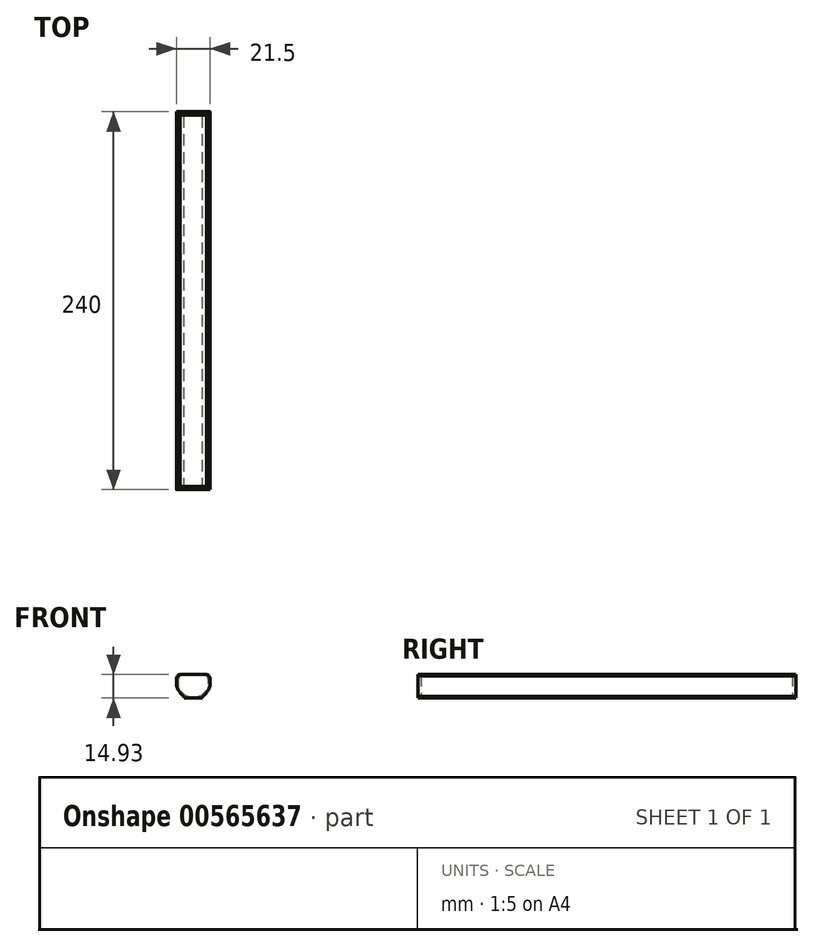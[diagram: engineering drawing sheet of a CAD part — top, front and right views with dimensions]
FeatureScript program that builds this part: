
annotation { "Feature Type Name" : "Feature", "Feature Type Description" : "" }
export const myFeature = defineFeature(function(context is Context, id is Id, definition is map)
    precondition{}
    {
        {
            var Q0;
            Q0=qCreatedBy(makeId("Front.planeOp"),FACE);
            var sketch = newSketch(context, id + "F0", { "sketchPlane" : qUnion([Q0])});
            skLineSegment(sketch, "E0", {"start": v(-4.53, -9.75) * mm, "end": v(4.53, -9.75) * mm});
            skPoint(sketch, "E1", {"position": v(0, -9.75) * mm});
            skArc(sketch, "E2", {"start": v(-8.5, 4.78) * mm, "mid": v(0, -9.75) * mm, "end": v(8.5, 4.78) * mm});
            skArc(sketch, "E3.0", {"start": v(-9.93, 4.1) * mm, "mid": v(-10.01, -3.9) * mm, "end": v(-4.53, -9.75) * mm});
            skArc(sketch, "E4.trimOffspring", {"start": v(4.53, -9.75) * mm, "mid": v(10.01, -3.9) * mm, "end": v(9.93, 4.1) * mm});
            skLineSegment(sketch, "E5", {"start": v(-9.93, 4.1) * mm, "end": v(-8.5, 4.78) * mm});
            skLineSegment(sketch, "E6", {"start": v(8.5, 4.78) * mm, "end": v(9.93, 4.1) * mm});
            skLineSegment(sketch, "E7", {"start": v(-6, -9.75) * mm, "end": v(-6, -8.92) * mm});
            skLineSegment(sketch, "E8", {"start": v(6, -9.75) * mm, "end": v(6, -8.92) * mm});
            skLineSegment(sketch, "E9.top", {"start": v(-6, -10.15) * mm, "end": v(6, -10.15) * mm});
            skLineSegment(sketch, "E9.left", {"start": v(-6, -9.75) * mm, "end": v(-6, -10.15) * mm});
            skLineSegment(sketch, "E9.right", {"start": v(6, -9.75) * mm, "end": v(6, -10.15) * mm});
            skLineSegment(sketch, "E10", {"start": v(-8.5, 4.78) * mm, "end": v(8.5, 4.78) * mm});
            skSolve(sketch);
        }
        {
            var Q0;
            {var subQ0=sQuery(id+"F0.wireOp",EDGE,"E5");Q0=makeQuery(id+"F0.imprint","IMPRINT",FACE,{"disambiguationData":[TD([[makeQuery(id+"F0.imprint","IMPRINT",EDGE,{"derivedFrom":subQ0}),-1.0]])]});}
            var Q1;
            {var subQ0=sQuery(id+"F0.wireOp",EDGE,"E6");Q1=makeQuery(id+"F0.imprint","IMPRINT",FACE,{"disambiguationData":[TD([[makeQuery(id+"F0.imprint","IMPRINT",EDGE,{"derivedFrom":subQ0}),-1.0]])]});}
            var Q2;
            {var subQ7=sQuery(id+"F0.wireOp",EDGE,"E7");Q2=makeQuery(id+"F0.imprint","IMPRINT",FACE,{"disambiguationData":[TD([[makeQuery(id+"F0.imprint","IMPRINT",EDGE,{"derivedFrom":subQ7}),-1.0]])]});}
            extrude(context, id + "F1", {"entities" : qUnion([Q0, Q1, Q2]), "depth" : 240 * mm, "offsetDistance" : 25 * mm});
        }
        {
            var Q0;
            {var subQ2=sQuery(id+"F0.wireOp",EDGE,"E10");Q0=makeQuery(id+"F0.imprint","IMPRINT",FACE,{"disambiguationData":[TD([[makeQuery(id+"F0.imprint","IMPRINT",EDGE,{"derivedFrom":subQ2}),-1.0]])]});}
            extrude(context, id + "F2", {"entities" : qUnion([Q0]), "operationType" : NewBodyOperationType.ADD, "depth" : 2 * mm, "offsetDistance" : 25 * mm});
        }
        {
            var Q0;
            Q0=makeQuery(id+"F1.opExtrude","CAP_FACE",FACE,{"disambiguationData":[OSD([sQuery(id+"F0.wireOp",EDGE,"E2"),sQuery(id+"F0.wireOp",EDGE,"E3.0"),sQuery(id+"F0.wireOp",EDGE,"E4.trimOffspring"),sQuery(id+"F0.wireOp",EDGE,"E5"),sQuery(id+"F0.wireOp",EDGE,"E6"),sQuery(id+"F0.wireOp",EDGE,"E7"),sQuery(id+"F0.wireOp",EDGE,"E8"),sQuery(id+"F0.wireOp",EDGE,"E9.top"),sQuery(id+"F0.wireOp",EDGE,"E9.left"),sQuery(id+"F0.wireOp",EDGE,"E9.right")])],"isStart":false});
            var sketch = newSketch(context, id + "F3", { "sketchPlane" : qUnion([Q0])});
            skLineSegment(sketch, "E11", {"start": v(-8.5, 4.78) * mm, "end": v(8.5, 4.78) * mm});
            skSolve(sketch);
        }
        {
            var Q0;
            Q0=makeQuery(id+"F3.imprint","IMPRINT",FACE,{"disambiguationData":[TD([[makeQuery(id+"F3.imprint","IMPRINT",EDGE,{"derivedFrom":sQuery(id+"F3.wireOp",EDGE,"E11")}),-1.0]])]});
            extrude(context, id + "F4", {"entities" : qUnion([Q0]), "operationType" : NewBodyOperationType.ADD, "oppositeDirection" : true, "depth" : 2 * mm, "offsetDistance" : 25 * mm});
        }
    });
